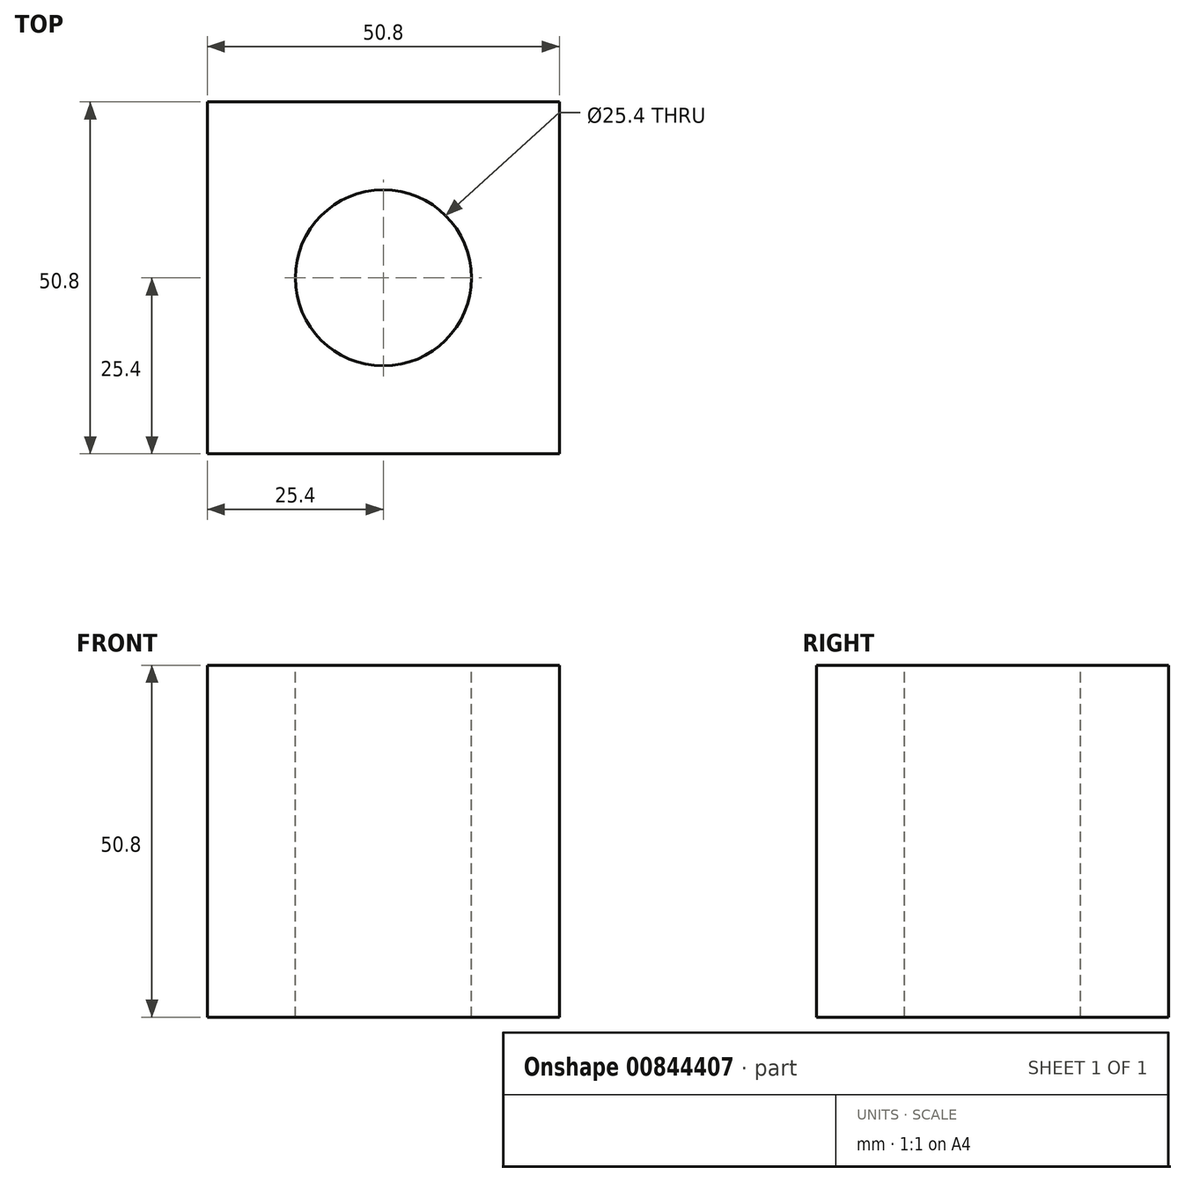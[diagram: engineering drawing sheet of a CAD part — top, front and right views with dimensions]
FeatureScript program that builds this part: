
annotation { "Feature Type Name" : "Feature", "Feature Type Description" : "" }
export const myFeature = defineFeature(function(context is Context, id is Id, definition is map)
    precondition{}
    {
        {
            var Q0;
            Q0=qCreatedBy(makeId("Top.planeOp"),FACE);
            var sketch = newSketch(context, id + "F0", { "sketchPlane" : qUnion([Q0])});
            skLineSegment(sketch, "E0.bottom", {"start": v(-25.4, 25.4) * mm, "end": v(25.4, 25.4) * mm});
            skLineSegment(sketch, "E0.top", {"start": v(-25.4, -25.4) * mm, "end": v(25.4, -25.4) * mm});
            skLineSegment(sketch, "E0.left", {"start": v(-25.4, 25.4) * mm, "end": v(-25.4, -25.4) * mm});
            skLineSegment(sketch, "E0.right", {"start": v(25.4, 25.4) * mm, "end": v(25.4, -25.4) * mm});
            skPoint(sketch, "E1", {"position": v(0, 25.4) * mm});
            skPoint(sketch, "E2", {"position": v(25.4, 0) * mm});
            skSolve(sketch);
        }
        {
            var Q0;
            Q0 = qSketchRegion(id + "F0", true);
            extrude(context, id + "F1", {"entities" : qUnion([Q0]), "endBound" : BoundingType.SYMMETRIC, "depth" : 50.8 * mm, "offsetDistance" : 25.4 * mm});
        }
        {
            var Q0;
            Q0=makeQuery(id+"F1.opExtrude","CAP_FACE",FACE,{"disambiguationData":[OSD([sQuery(id+"F0.wireOp",EDGE,"E0.bottom"),sQuery(id+"F0.wireOp",EDGE,"E0.top"),sQuery(id+"F0.wireOp",EDGE,"E0.left"),sQuery(id+"F0.wireOp",EDGE,"E0.right")])],"isStart":false});
            var sketch = newSketch(context, id + "F2", { "sketchPlane" : qUnion([Q0])});
            skCircle(sketch, "E3", {"center": v(0, 0) * mm, "radius": 12.7 * mm});
            skSolve(sketch);
        }
        {
            var Q0;
            Q0 = qSketchRegion(id + "F2", true);
            var Q1;
            Q1=makeQuery(id+"F1.opExtrude","CAP_FACE",FACE,{"disambiguationData":[OSD([sQuery(id+"F0.wireOp",EDGE,"E0.bottom"),sQuery(id+"F0.wireOp",EDGE,"E0.top"),sQuery(id+"F0.wireOp",EDGE,"E0.left"),sQuery(id+"F0.wireOp",EDGE,"E0.right")])],"isStart":true});
            extrude(context, id + "F3", {"entities" : qUnion([Q0]), "operationType" : NewBodyOperationType.REMOVE, "endBound" : BoundingType.UP_TO_SURFACE, "oppositeDirection" : true, "depth" : 25.4 * mm, "endBoundEntityFace" : qUnion([Q1]), "offsetDistance" : 25.4 * mm});
        }
    });
